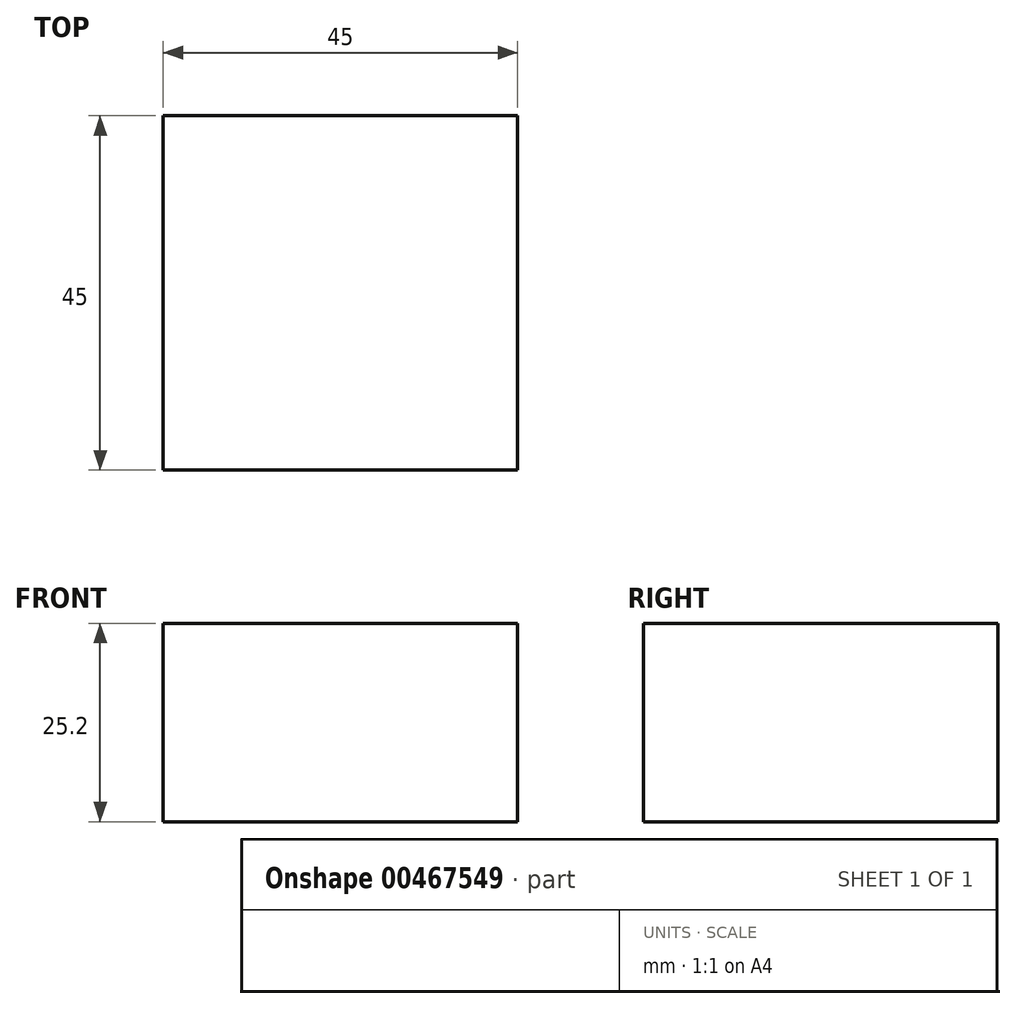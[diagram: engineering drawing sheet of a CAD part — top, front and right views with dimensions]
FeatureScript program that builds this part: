
annotation { "Feature Type Name" : "Feature", "Feature Type Description" : "" }
export const myFeature = defineFeature(function(context is Context, id is Id, definition is map)
    precondition{}
    {
        {
            var Q0;
            Q0=qCreatedBy(makeId("Top.planeOp"),FACE);
            var sketch = newSketch(context, id + "F0", { "sketchPlane" : qUnion([Q0])});
            skLineSegment(sketch, "E0.bottom", {"start": v(0, 0) * mm, "end": v(45, 0) * mm});
            skLineSegment(sketch, "E0.top", {"start": v(0, 45) * mm, "end": v(45, 45) * mm});
            skLineSegment(sketch, "E0.left", {"start": v(0, 0) * mm, "end": v(0, 45) * mm});
            skLineSegment(sketch, "E0.right", {"start": v(45, 0) * mm, "end": v(45, 45) * mm});
            skSolve(sketch);
        }
        {
            var Q0;
            Q0=qSketchRegion(id+"F0",true);
            extrude(context, id + "F1", {"entities" : qUnion([Q0]), "depth" : 12 * 2.1 * mm});
        }
    });
